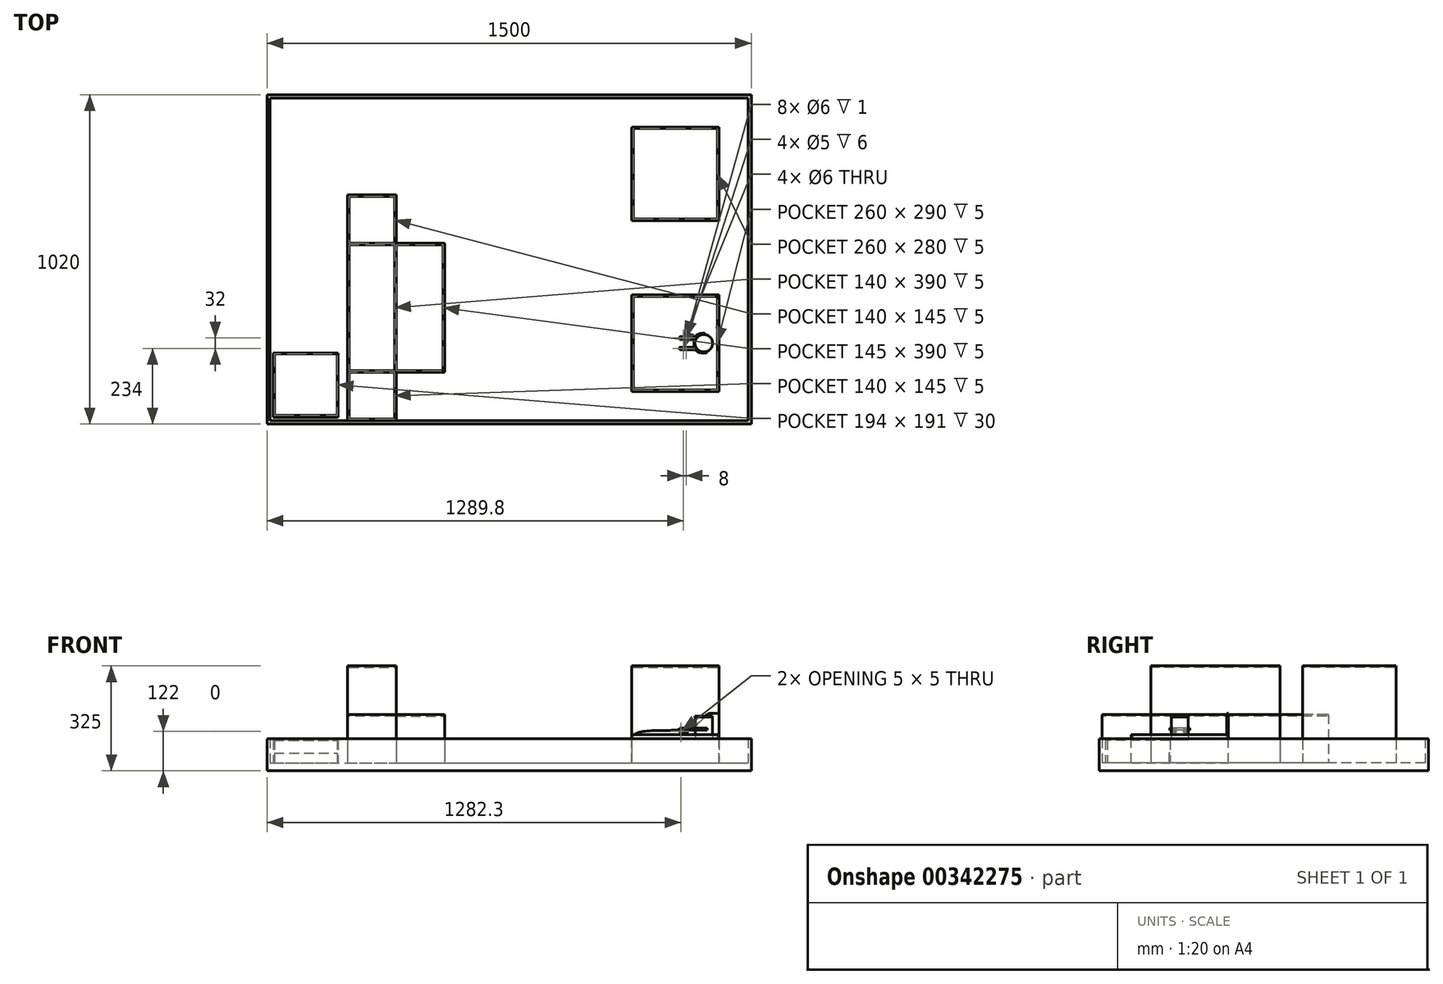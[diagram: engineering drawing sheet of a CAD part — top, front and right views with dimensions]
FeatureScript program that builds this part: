
annotation { "Feature Type Name" : "Feature", "Feature Type Description" : "" }
export const myFeature = defineFeature(function(context is Context, id is Id, definition is map)
    precondition{}
    {
        {
            var Q0;
            Q0=qCreatedBy(makeId("Top.planeOp"),FACE);
            var sketch = newSketch(context, id + "F0", { "sketchPlane" : qUnion([Q0])});
            skCircle(sketch, "E0", {"center": v(0, 0) * mm, "radius": 27.2 * mm});
            skSolve(sketch);
        }
        {
            var Q0;
            Q0=qSketchRegion(id+"F0",true);
            extrude(context, id + "F1", {"entities" : qUnion([Q0]), "depth" : 2.83 * mm});
        }
        {
            var Q0;
            Q0=makeQuery(id+"F1.opExtrude","CAP_FACE",FACE,{"disambiguationData":[OSD([sQuery(id+"F0.wireOp",EDGE,"E0")])],"isStart":false});
            var sketch = newSketch(context, id + "F2", { "sketchPlane" : qUnion([Q0])});
            skCircle(sketch, "E1", {"center": v(0, 0) * mm, "radius": 26.4 * mm});
            skSolve(sketch);
        }
        {
            var Q0;
            Q0=qSketchRegion(id+"F2",true);
            extrude(context, id + "F3", {"entities" : qUnion([Q0]), "operationType" : NewBodyOperationType.ADD, "depth" : 67.36 * mm});
        }
        {
            var Q0;
            Q0=makeQuery(id+"F3.opExtrude","CAP_FACE",FACE,{"disambiguationData":[OSD([sQuery(id+"F2.wireOp",EDGE,"E1")])],"isStart":false});
            var sketch = newSketch(context, id + "F4", { "sketchPlane" : qUnion([Q0])});
            skCircle(sketch, "E2", {"center": v(0, 0) * mm, "radius": 27.2 * mm});
            skSolve(sketch);
        }
        {
            var Q0;
            Q0=qSketchRegion(id+"F4",true);
            extrude(context, id + "F5", {"entities" : qUnion([Q0]), "operationType" : NewBodyOperationType.ADD, "depth" : 2.83 * mm});
        }
        {
            var Q0;
            Q0=makeQuery(id+"F5.opExtrude","CAP_FACE",FACE,{"disambiguationData":[OSD([sQuery(id+"F4.wireOp",EDGE,"E2")])],"isStart":false});
            var sketch = newSketch(context, id + "F6", { "sketchPlane" : qUnion([Q0])});
            skSolve(sketch);
        }
        {
            var Q0;
            Q0=qCreatedBy(makeId("Top.planeOp"),FACE);
            cPlane(context, id + "F7", {"entities" : qUnion([Q0]), "cplaneType" : CPlaneType.OFFSET, "offset" : 25 * mm, "width" : 150 * mm, "height" : 150 * mm});
        }
        {
            var Q0;
            Q0=makeQuery(id+"F6.imprint","IMPRINT",FACE,{"disambiguationData":[TD([[makeQuery(id+"F6.imprint","IMPRINT",EDGE,{"derivedFrom":makeQuery(id+"F5.opExtrude","CAP_EDGE",EDGE,{"disambiguationData":[OSD([sQuery(id+"F4.wireOp",EDGE,"E2")])],"isStart":false})}),1.0]])]});
            var sketch = newSketch(context, id + "F8", { "sketchPlane" : qUnion([Q0])});
            skSolve(sketch);
        }
        {
            var Q0;
            Q0=qCreatedBy(makeId("Top.planeOp"),FACE);
            var sketch = newSketch(context, id + "F9", { "sketchPlane" : qUnion([Q0])});
            skLineSegment(sketch, "E3.bottom", {"start": v(-222.8, -150) * mm, "end": v(47.2, -150) * mm});
            skLineSegment(sketch, "E3.top", {"start": v(-222.8, 150) * mm, "end": v(47.2, 150) * mm});
            skLineSegment(sketch, "E3.left", {"start": v(-222.8, -150) * mm, "end": v(-222.8, 150) * mm});
            skLineSegment(sketch, "E3.right", {"start": v(47.2, -150) * mm, "end": v(47.2, 150) * mm});
            skSolve(sketch);
        }
        {
            var Q0;
            Q0=qSketchRegion(id+"F9",true);
            extrude(context, id + "F10", {"entities" : qUnion([Q0]), "oppositeDirection" : true, "depth" : 72 * mm});
        }
        {
            var Q0;
            Q0=makeQuery(id+"F10.opExtrude","CAP_FACE",FACE,{"disambiguationData":[OSD([sQuery(id+"F9.wireOp",EDGE,"E3.bottom"),sQuery(id+"F9.wireOp",EDGE,"E3.top"),sQuery(id+"F9.wireOp",EDGE,"E3.left"),sQuery(id+"F9.wireOp",EDGE,"E3.right")])],"isStart":true});
            var sketch = newSketch(context, id + "F11", { "sketchPlane" : qUnion([Q0])});
            skLineSegment(sketch, "E4.bottom", {"start": v(-222.8, -150) * mm, "end": v(47.2, -150) * mm});
            skLineSegment(sketch, "E4.top", {"start": v(-222.8, -145) * mm, "end": v(42.2, -145) * mm});
            skLineSegment(sketch, "E4.left", {"start": v(-222.8, -150) * mm, "end": v(-222.8, -145) * mm});
            skLineSegment(sketch, "E5.bottom", {"start": v(47.2, 150) * mm, "end": v(42.2, 150) * mm});
            skLineSegment(sketch, "E5.left", {"start": v(47.2, 150) * mm, "end": v(47.2, -150) * mm});
            skLineSegment(sketch, "E5.right", {"start": v(42.2, 150) * mm, "end": v(42.2, -145) * mm});
            skSolve(sketch);
        }
        {
            var Q0;
            Q0=qSketchRegion(id+"F11",true);
            extrude(context, id + "F12", {"entities" : qUnion([Q0]), "operationType" : NewBodyOperationType.ADD, "depth" : 15 * mm});
        }
        {
            var Q0;
            Q0=makeQuery(id+"F12.boolean.opBoolean","MERGE",FACE,{"derivedFrom":[makeQuery(id+"F10.opExtrude","SWEPT_FACE",FACE,{"disambiguationData":[OSD([sQuery(id+"F9.wireOp",EDGE,"E3.top")])]}),makeQuery(id+"F12.opExtrude","SWEPT_FACE",FACE,{"disambiguationData":[OSD([sQuery(id+"F11.wireOp",EDGE,"E5.bottom")])]})]});
            var sketch = newSketch(context, id + "F13", { "sketchPlane" : qUnion([Q0])});
            skLineSegment(sketch, "E6", {"start": v(-47.2, 81.36) * mm, "end": v(-21.31, 81.36) * mm});
            skFitSpline(sketch, "E7", {"points": [v(-21.31, 81.36) * mm, v(15.24, 52.01) * mm, v(114.14, 28.17) * mm, v(222.8, 0) * mm], "startDerivative": vector(181.02, 0.3) * mm, "endDerivative": vector(-1.73, -239.85) * mm});
            skLineSegment(sketch, "E8", {"start": v(-47.2, 81.36) * mm, "end": v(-47.2, -72) * mm});
            skLineSegment(sketch, "E9", {"start": v(-47.2, -72) * mm, "end": v(222.8, -72) * mm});
            skLineSegment(sketch, "E10", {"start": v(222.8, -72) * mm, "end": v(222.8, 0) * mm});
            skSolve(sketch);
        }
        {
            var Q0;
            Q0=qSketchRegion(id+"F13",true);
            extrude(context, id + "F14", {"entities" : qUnion([Q0]), "operationType" : NewBodyOperationType.ADD, "oppositeDirection" : true, "depth" : 5 * mm});
        }
        {
            var Q0;
            Q0=makeQuery(id+"F10.opExtrude","CAP_FACE",FACE,{"disambiguationData":[OSD([sQuery(id+"F9.wireOp",EDGE,"E3.bottom"),sQuery(id+"F9.wireOp",EDGE,"E3.top"),sQuery(id+"F9.wireOp",EDGE,"E3.left"),sQuery(id+"F9.wireOp",EDGE,"E3.right")])],"isStart":true});
            var sketch = newSketch(context, id + "F15", { "sketchPlane" : qUnion([Q0])});
            skLineSegment(sketch, "E11.bottom", {"start": v(-222.8, 145) * mm, "end": v(-217.8, 145) * mm});
            skLineSegment(sketch, "E11.top", {"start": v(-222.8, -145) * mm, "end": v(-217.8, -145) * mm});
            skLineSegment(sketch, "E11.left", {"start": v(-222.8, 145) * mm, "end": v(-222.8, -145) * mm});
            skLineSegment(sketch, "E11.right", {"start": v(-217.8, 145) * mm, "end": v(-217.8, -145) * mm});
            skSolve(sketch);
        }
        {
            var Q0;
            Q0=qSketchRegion(id+"F15",true);
            extrude(context, id + "F16", {"entities" : qUnion([Q0]), "operationType" : NewBodyOperationType.ADD, "depth" : 5 * mm});
        }
        {
            var Q0;
            Q0=makeQuery(id+"F10.opExtrude","CAP_FACE",FACE,{"disambiguationData":[OSD([sQuery(id+"F9.wireOp",EDGE,"E3.bottom"),sQuery(id+"F9.wireOp",EDGE,"E3.top"),sQuery(id+"F9.wireOp",EDGE,"E3.left"),sQuery(id+"F9.wireOp",EDGE,"E3.right")])],"isStart":false});
            var sketch = newSketch(context, id + "F17", { "sketchPlane" : qUnion([Q0])});
            skLineSegment(sketch, "E12.bottom", {"start": v(147.2, 250) * mm, "end": v(-1352.8, 250) * mm});
            skLineSegment(sketch, "E12.top", {"start": v(147.2, -770) * mm, "end": v(-1352.8, -770) * mm});
            skLineSegment(sketch, "E12.left", {"start": v(147.2, 250) * mm, "end": v(147.2, -770) * mm});
            skLineSegment(sketch, "E12.right", {"start": v(-1352.8, 250) * mm, "end": v(-1352.8, -770) * mm});
            skSolve(sketch);
        }
        {
            var Q0;
            Q0=qSketchRegion(id+"F17",true);
            extrude(context, id + "F18", {"entities" : qUnion([Q0]), "operationType" : NewBodyOperationType.ADD, "depth" : 25 * mm});
        }
        {
            var Q0;
            Q0=makeQuery(id+"F18.opExtrude","CAP_FACE",FACE,{"disambiguationData":[OSD([sQuery(id+"F17.wireOp",EDGE,"E12.bottom"),sQuery(id+"F17.wireOp",EDGE,"E12.top"),sQuery(id+"F17.wireOp",EDGE,"E12.left"),sQuery(id+"F17.wireOp",EDGE,"E12.right")])],"isStart":true});
            var sketch = newSketch(context, id + "F19", { "sketchPlane" : qUnion([Q0])});
            skLineSegment(sketch, "E13.bottom", {"start": v(-222.8, 670) * mm, "end": v(47.2, 670) * mm});
            skLineSegment(sketch, "E13.top", {"start": v(-222.8, 380) * mm, "end": v(47.2, 380) * mm});
            skLineSegment(sketch, "E13.left", {"start": v(-222.8, 670) * mm, "end": v(-222.8, 380) * mm});
            skLineSegment(sketch, "E13.right", {"start": v(47.2, 670) * mm, "end": v(47.2, 380) * mm});
            skSolve(sketch);
        }
        {
            var Q0;
            Q0=qSketchRegion(id+"F19",true);
            extrude(context, id + "F20", {"entities" : qUnion([Q0]), "operationType" : NewBodyOperationType.ADD, "depth" : 300 * mm});
        }
        {
            var Q0;
            Q0=makeQuery(id+"F20.opExtrude","CAP_FACE",FACE,{"disambiguationData":[OSD([sQuery(id+"F19.wireOp",EDGE,"E13.bottom"),sQuery(id+"F19.wireOp",EDGE,"E13.top"),sQuery(id+"F19.wireOp",EDGE,"E13.left"),sQuery(id+"F19.wireOp",EDGE,"E13.right")])],"isStart":false});
            var sketch = newSketch(context, id + "F21", { "sketchPlane" : qUnion([Q0])});
            skLineSegment(sketch, "E14.bottom", {"start": v(-217.8, 665) * mm, "end": v(42.2, 665) * mm});
            skLineSegment(sketch, "E14.top", {"start": v(-217.8, 385) * mm, "end": v(42.2, 385) * mm});
            skLineSegment(sketch, "E14.left", {"start": v(-217.8, 665) * mm, "end": v(-217.8, 385) * mm});
            skLineSegment(sketch, "E14.right", {"start": v(42.2, 665) * mm, "end": v(42.2, 385) * mm});
            skSolve(sketch);
        }
        {
            var Q0;
            Q0=qSketchRegion(id+"F21",true);
            extrude(context, id + "F22", {"entities" : qUnion([Q0]), "operationType" : NewBodyOperationType.REMOVE, "oppositeDirection" : true, "depth" : 5 * mm});
        }
        {
            var Q0;
            Q0=makeQuery(id+"F18.opExtrude","CAP_FACE",FACE,{"disambiguationData":[OSD([sQuery(id+"F17.wireOp",EDGE,"E12.bottom"),sQuery(id+"F17.wireOp",EDGE,"E12.top"),sQuery(id+"F17.wireOp",EDGE,"E12.left"),sQuery(id+"F17.wireOp",EDGE,"E12.right")])],"isStart":true});
            var sketch = newSketch(context, id + "F23", { "sketchPlane" : qUnion([Q0])});
            skLineSegment(sketch, "E15.bottom", {"start": v(-1352.8, 770) * mm, "end": v(147.2, 770) * mm});
            skLineSegment(sketch, "E15.top", {"start": v(-1352.8, -250) * mm, "end": v(147.2, -250) * mm});
            skLineSegment(sketch, "E15.left", {"start": v(-1352.8, 770) * mm, "end": v(-1352.8, -250) * mm});
            skLineSegment(sketch, "E15.right", {"start": v(147.2, 770) * mm, "end": v(147.2, -250) * mm});
            skLineSegment(sketch, "E16.bottom", {"start": v(-1342.8, 760) * mm, "end": v(137.2, 760) * mm});
            skLineSegment(sketch, "E16.top", {"start": v(-1342.8, -240) * mm, "end": v(137.2, -240) * mm});
            skLineSegment(sketch, "E16.left", {"start": v(-1342.8, 760) * mm, "end": v(-1342.8, -240) * mm});
            skLineSegment(sketch, "E16.right", {"start": v(137.2, 760) * mm, "end": v(137.2, -240) * mm});
            skSolve(sketch);
        }
        {
            var Q0;
            Q0=qSketchRegion(id+"F23",true);
            extrude(context, id + "F24", {"entities" : qUnion([Q0]), "operationType" : NewBodyOperationType.ADD, "depth" : 75 * mm});
        }
        {
            var Q0;
            Q0=makeQuery(id+"F18.opExtrude","CAP_FACE",FACE,{"disambiguationData":[OSD([sQuery(id+"F17.wireOp",EDGE,"E12.bottom"),sQuery(id+"F17.wireOp",EDGE,"E12.top"),sQuery(id+"F17.wireOp",EDGE,"E12.left"),sQuery(id+"F17.wireOp",EDGE,"E12.right")])],"isStart":true});
            var sketch = newSketch(context, id + "F25", { "sketchPlane" : qUnion([Q0])});
            skLineSegment(sketch, "E17.bottom", {"start": v(-1102.8, 460) * mm, "end": v(-952.8, 460) * mm});
            skLineSegment(sketch, "E17.top", {"start": v(-1102.8, -240) * mm, "end": v(-952.8, -240) * mm});
            skLineSegment(sketch, "E17.left", {"start": v(-1102.8, 460) * mm, "end": v(-1102.8, -240) * mm});
            skLineSegment(sketch, "E17.right", {"start": v(-952.8, 460) * mm, "end": v(-952.8, 310) * mm});
            skLineSegment(sketch, "E18.bottom", {"start": v(-952.8, 310) * mm, "end": v(-802.8, 310) * mm});
            skLineSegment(sketch, "E18.top", {"start": v(-952.8, -90) * mm, "end": v(-802.8, -90) * mm});
            skLineSegment(sketch, "E18.right", {"start": v(-802.8, 310) * mm, "end": v(-802.8, -90) * mm});
            skLineSegment(sketch, "E19.trimOffspring", {"start": v(-952.8, -90) * mm, "end": v(-952.8, -240) * mm});
            skSolve(sketch);
        }
        {
            var Q0;
            Q0=qSketchRegion(id+"F25",true);
            extrude(context, id + "F26", {"entities" : qUnion([Q0]), "operationType" : NewBodyOperationType.ADD, "depth" : 150 * mm});
        }
        {
            var Q0;
            Q0=makeQuery(id+"F26.opExtrude","CAP_FACE",FACE,{"disambiguationData":[OSD([sQuery(id+"F25.wireOp",EDGE,"E17.bottom"),sQuery(id+"F25.wireOp",EDGE,"E17.top"),sQuery(id+"F25.wireOp",EDGE,"E17.left"),sQuery(id+"F25.wireOp",EDGE,"E17.right"),sQuery(id+"F25.wireOp",EDGE,"E18.bottom"),sQuery(id+"F25.wireOp",EDGE,"E18.top"),sQuery(id+"F25.wireOp",EDGE,"E18.right"),sQuery(id+"F25.wireOp",EDGE,"E19.trimOffspring")])],"isStart":false});
            var sketch = newSketch(context, id + "F27", { "sketchPlane" : qUnion([Q0])});
            skLineSegment(sketch, "E20.bottom", {"start": v(-952.8, 310) * mm, "end": v(-1102.8, 310) * mm});
            skLineSegment(sketch, "E20.top", {"start": v(-952.8, -90) * mm, "end": v(-1102.8, -90) * mm});
            skLineSegment(sketch, "E20.left", {"start": v(-952.8, 310) * mm, "end": v(-952.8, -90) * mm});
            skLineSegment(sketch, "E20.right", {"start": v(-1102.8, 310) * mm, "end": v(-1102.8, -90) * mm});
            skSolve(sketch);
        }
        {
            var Q0;
            Q0=qSketchRegion(id+"F27",true);
            extrude(context, id + "F28", {"entities" : qUnion([Q0]), "operationType" : NewBodyOperationType.ADD, "depth" : 150 * mm});
        }
        {
            var Q0;
            Q0=makeQuery(id+"F28.opExtrude","CAP_FACE",FACE,{"disambiguationData":[OSD([sQuery(id+"F27.wireOp",EDGE,"E20.bottom"),sQuery(id+"F27.wireOp",EDGE,"E20.top"),sQuery(id+"F27.wireOp",EDGE,"E20.left"),sQuery(id+"F27.wireOp",EDGE,"E20.right")])],"isStart":false});
            var sketch = newSketch(context, id + "F29", { "sketchPlane" : qUnion([Q0])});
            skLineSegment(sketch, "E21.bottom", {"start": v(-1097.8, 305) * mm, "end": v(-957.8, 305) * mm});
            skLineSegment(sketch, "E21.top", {"start": v(-1097.8, -85) * mm, "end": v(-957.8, -85) * mm});
            skLineSegment(sketch, "E21.left", {"start": v(-1097.8, 305) * mm, "end": v(-1097.8, -85) * mm});
            skLineSegment(sketch, "E21.right", {"start": v(-957.8, 305) * mm, "end": v(-957.8, -85) * mm});
            skSolve(sketch);
        }
        {
            var Q0;
            Q0=qSketchRegion(id+"F29",true);
            extrude(context, id + "F30", {"entities" : qUnion([Q0]), "operationType" : NewBodyOperationType.REMOVE, "oppositeDirection" : true, "depth" : 5 * mm});
        }
        {
            var Q0;
            {var subQ0=sQuery(id+"F25.wireOp",EDGE,"E17.left");var subQ1=sQuery(id+"F25.wireOp",EDGE,"E18.bottom");var subQ2=sQuery(id+"F25.wireOp",EDGE,"E17.right");var subQ3=sQuery(id+"F25.wireOp",EDGE,"E17.bottom");var subQ4=makeQuery(id+"F26.opExtrude","CAP_FACE",FACE,{"disambiguationData":[OSD([subQ3,sQuery(id+"F25.wireOp",EDGE,"E17.top"),subQ0,subQ2,subQ1,sQuery(id+"F25.wireOp",EDGE,"E18.top"),sQuery(id+"F25.wireOp",EDGE,"E18.right"),sQuery(id+"F25.wireOp",EDGE,"E19.trimOffspring")])],"isStart":false});Q0=makeQuery(id+"F28.boolean.opBoolean","SPLIT",FACE,{"disambiguationData":[TD([makeQuery(id+"F26.opExtrude","SWEPT_FACE",FACE,{"disambiguationData":[OSD([subQ3])]})])],"derivedFrom":subQ4});}
            var sketch = newSketch(context, id + "F31", { "sketchPlane" : qUnion([Q0])});
            skLineSegment(sketch, "E22.bottom", {"start": v(-1097.8, 455) * mm, "end": v(-957.8, 455) * mm});
            skLineSegment(sketch, "E22.top", {"start": v(-1097.8, 310) * mm, "end": v(-957.8, 310) * mm});
            skLineSegment(sketch, "E22.left", {"start": v(-1097.8, 455) * mm, "end": v(-1097.8, 310) * mm});
            skLineSegment(sketch, "E22.right", {"start": v(-957.8, 455) * mm, "end": v(-957.8, 310) * mm});
            skLineSegment(sketch, "E23.bottom", {"start": v(-952.8, 305) * mm, "end": v(-807.8, 305) * mm});
            skLineSegment(sketch, "E23.top", {"start": v(-952.8, -85) * mm, "end": v(-807.8, -85) * mm});
            skLineSegment(sketch, "E23.left", {"start": v(-952.8, 305) * mm, "end": v(-952.8, -85) * mm});
            skLineSegment(sketch, "E23.right", {"start": v(-807.8, 305) * mm, "end": v(-807.8, -85) * mm});
            skLineSegment(sketch, "E24.bottom", {"start": v(-1097.8, -90) * mm, "end": v(-957.8, -90) * mm});
            skLineSegment(sketch, "E24.top", {"start": v(-1097.8, -235) * mm, "end": v(-957.8, -235) * mm});
            skLineSegment(sketch, "E24.left", {"start": v(-1097.8, -90) * mm, "end": v(-1097.8, -235) * mm});
            skLineSegment(sketch, "E24.right", {"start": v(-957.8, -90) * mm, "end": v(-957.8, -235) * mm});
            skSolve(sketch);
        }
        {
            var Q0;
            Q0=qSketchRegion(id+"F31",true);
            extrude(context, id + "F32", {"entities" : qUnion([Q0]), "operationType" : NewBodyOperationType.REMOVE, "oppositeDirection" : true, "depth" : 5 * mm});
        }
        {
            var Q0;
            Q0=qCreatedBy(id+"F7.planeOp",FACE);
            var sketch = newSketch(context, id + "F33", { "sketchPlane" : qUnion([Q0])});
            skLineSegment(sketch, "E25", {"start": v(0, 0) * mm, "end": v(-90, 0) * mm, "construction": true});
            skLineSegment(sketch, "E26.bottom", {"start": v(-74.5, -12) * mm, "end": v(-55, -12) * mm});
            skLineSegment(sketch, "E26.top", {"start": v(-74.5, -20) * mm, "end": v(-55, -20) * mm});
            skLineSegment(sketch, "E26.left", {"start": v(-74.5, -12) * mm, "end": v(-74.5, -13) * mm});
            skPoint(sketch, "E27.visualSharp", {"position": v(-51, -12) * mm});
            skPoint(sketch, "E28.visualSharp", {"position": v(-51, -20) * mm});
            skCircle(sketch, "E29", {"center": v(-55, -16) * mm, "radius": 3 * mm});
            skLineSegment(sketch, "E30", {"start": v(-59, -3.98) * mm, "end": v(-59, -18.08) * mm, "construction": true});
            skCircle(sketch, "E31.MirrorC", {"center": v(-63, -16) * mm, "radius": 3 * mm});
            skLineSegment(sketch, "E32.bottom", {"start": v(-74.5, -13) * mm, "end": v(-65.65, -13) * mm});
            skLineSegment(sketch, "E32.top", {"start": v(-74.5, -19) * mm, "end": v(-65.65, -19) * mm});
            skArc(sketch, "E33", {"start": v(-65.65, -13) * mm, "mid": v(-67, -16) * mm, "end": v(-65.65, -19) * mm});
            skLineSegment(sketch, "E34.trimOffspring", {"start": v(-74.5, -19) * mm, "end": v(-74.5, -20) * mm});
            skArc(sketch, "E35.trimOffspring", {"start": v(-55, -20) * mm, "mid": v(-51, -16) * mm, "end": v(-55, -12) * mm});
            skLineSegment(sketch, "E36.MirrorCS", {"start": v(-74.5, 12) * mm, "end": v(-74.5, 13) * mm});
            skLineSegment(sketch, "E37.MirrorCS", {"start": v(-74.5, 19) * mm, "end": v(-74.5, 20) * mm});
            skPoint(sketch, "E38.MirrorP", {"position": v(-51, 12) * mm});
            skLineSegment(sketch, "E39.MirrorCS", {"start": v(-74.5, 12) * mm, "end": v(-55, 12) * mm});
            skPoint(sketch, "E40.MirrorP", {"position": v(-51, 20) * mm});
            skArc(sketch, "E41.MirrorCS", {"start": v(-65.65, 13) * mm, "mid": v(-67, 16) * mm, "end": v(-65.65, 19) * mm});
            skArc(sketch, "E42.MirrorCS", {"start": v(-55, 20) * mm, "mid": v(-51, 16) * mm, "end": v(-55, 12) * mm});
            skLineSegment(sketch, "E43.MirrorCS", {"start": v(-74.5, 20) * mm, "end": v(-55, 20) * mm});
            skCircle(sketch, "E44.MirrorC", {"center": v(-55, 16) * mm, "radius": 3 * mm});
            skCircle(sketch, "E45.MirrorC", {"center": v(-63, 16) * mm, "radius": 3 * mm});
            skLineSegment(sketch, "E46.MirrorCS", {"start": v(-74.5, 19) * mm, "end": v(-65.65, 19) * mm});
            skLineSegment(sketch, "E47.MirrorCS", {"start": v(-74.5, 13) * mm, "end": v(-65.65, 13) * mm});
            skSolve(sketch);
        }
        {
            var Q0;
            Q0=qSketchRegion(id+"F33",true);
            var Q1;
            Q1=qSketchRegion(id+"F36",true);
            extrude(context, id + "F34", {"entities" : qUnion([Q0, Q1]), "endBound" : BoundingType.SYMMETRIC, "depth" : 8 * mm});
        }
        {
            var Q0;
            Q0=makeQuery(id+"F34.opExtrude","CAP_EDGE",EDGE,{"disambiguationData":[OSD([sQuery(id+"F33.wireOp",EDGE,"E34.trimOffspring")])],"isStart":false});
            var Q1;
            Q1=makeQuery(id+"F34.opExtrude","CAP_EDGE",EDGE,{"disambiguationData":[OSD([sQuery(id+"F33.wireOp",EDGE,"E26.left")])],"isStart":false});
            var Q2;
            Q2=makeQuery(id+"F34.opExtrude","CAP_EDGE",EDGE,{"disambiguationData":[OSD([sQuery(id+"F33.wireOp",EDGE,"E34.trimOffspring")])],"isStart":true});
            var Q3;
            Q3=makeQuery(id+"F34.opExtrude","CAP_EDGE",EDGE,{"disambiguationData":[OSD([sQuery(id+"F33.wireOp",EDGE,"E26.left")])],"isStart":true});
            var Q4;
            Q4=makeQuery(id+"F34.opExtrude","CAP_EDGE",EDGE,{"disambiguationData":[OSD([sQuery(id+"F33.wireOp",EDGE,"E36.MirrorCS")])],"isStart":false});
            var Q5;
            Q5=makeQuery(id+"F34.opExtrude","CAP_EDGE",EDGE,{"disambiguationData":[OSD([sQuery(id+"F33.wireOp",EDGE,"E37.MirrorCS")])],"isStart":false});
            var Q6;
            Q6=makeQuery(id+"F34.opExtrude","CAP_EDGE",EDGE,{"disambiguationData":[OSD([sQuery(id+"F33.wireOp",EDGE,"E37.MirrorCS")])],"isStart":true});
            var Q7;
            Q7=makeQuery(id+"F34.opExtrude","CAP_EDGE",EDGE,{"disambiguationData":[OSD([sQuery(id+"F33.wireOp",EDGE,"E36.MirrorCS")])],"isStart":true});
            fillet(context, id + "F35", {"entities" : qUnion([Q0, Q1, Q2, Q3, Q4, Q5, Q6, Q7]), "radius" : 4 * mm, "tangentPropagation" : true, "allowEdgeOverflow" : false});
        }
        {
            var Q0;
            Q0=makeQuery(id+"F34.opExtrude","SWEPT_FACE",FACE,{"disambiguationData":[OSD([sQuery(id+"F33.wireOp",EDGE,"E26.top")])]});
            var sketch = newSketch(context, id + "F36", { "sketchPlane" : qUnion([Q0])});
            skCircle(sketch, "E48", {"center": v(-70.5, 25) * mm, "radius": 3 * mm});
            skSolve(sketch);
        }
        {
            var Q0;
            Q0=qSketchRegion(id+"F36",true);
            var Q1;
            Q1=makeQuery(id+"F34.opExtrude","SWEPT_FACE",FACE,{"disambiguationData":[OSD([sQuery(id+"F33.wireOp",EDGE,"E26.bottom")])]});
            extrude(context, id + "F37", {"entities" : qUnion([Q0]), "operationType" : NewBodyOperationType.ADD, "endBound" : BoundingType.UP_TO_SURFACE, "oppositeDirection" : true, "endBoundEntityFace" : qUnion([Q1]), "depth" : 25 * mm});
        }
        {
            var Q0;
            Q0=makeQuery(id+"F34.opExtrude","SWEPT_FACE",FACE,{"disambiguationData":[OSD([sQuery(id+"F33.wireOp",EDGE,"E43.MirrorCS")])]});
            var sketch = newSketch(context, id + "F38", { "sketchPlane" : qUnion([Q0])});
            skCircle(sketch, "E49", {"center": v(70.5, 25) * mm, "radius": 3 * mm});
            skSolve(sketch);
        }
        {
            var Q0;
            Q0=qSketchRegion(id+"F38",true);
            var Q1;
            Q1=makeQuery(id+"F34.opExtrude","SWEPT_FACE",FACE,{"disambiguationData":[OSD([sQuery(id+"F33.wireOp",EDGE,"E39.MirrorCS")])]});
            extrude(context, id + "F39", {"entities" : qUnion([Q0]), "operationType" : NewBodyOperationType.ADD, "endBound" : BoundingType.UP_TO_SURFACE, "oppositeDirection" : true, "endBoundEntityFace" : qUnion([Q1]), "depth" : 25 * mm});
        }
        {
            var Q0;
            Q0=qCreatedBy(id+"F7.planeOp",FACE);
            var sketch = newSketch(context, id + "F40", { "sketchPlane" : qUnion([Q0])});
            skCircle(sketch, "E50", {"center": v(-55, 16) * mm, "radius": 3 * mm});
            skCircle(sketch, "E51", {"center": v(-63, 16) * mm, "radius": 2.5 * mm});
            skCircle(sketch, "E52", {"center": v(-63, 16) * mm, "radius": 3 * mm});
            skCircle(sketch, "E53", {"center": v(-55, 16) * mm, "radius": 2.5 * mm});
            skSolve(sketch);
        }
        {
            var Q0;
            Q0=qSketchRegion(id+"F40",true);
            extrude(context, id + "F41", {"entities" : qUnion([Q0]), "operationType" : NewBodyOperationType.ADD, "endBound" : BoundingType.SYMMETRIC, "depth" : 6 * mm});
        }
        {
            var Q0;
            Q0=qCreatedBy(id+"F7.planeOp",FACE);
            var sketch = newSketch(context, id + "F42", { "sketchPlane" : qUnion([Q0])});
            skCircle(sketch, "E54", {"center": v(-63, -16) * mm, "radius": 2.5 * mm});
            skCircle(sketch, "E55", {"center": v(-63, -16) * mm, "radius": 3 * mm});
            skCircle(sketch, "E56", {"center": v(-55, -16) * mm, "radius": 2.5 * mm});
            skCircle(sketch, "E57", {"center": v(-55, -16) * mm, "radius": 3 * mm});
            skSolve(sketch);
        }
        {
            var Q0;
            Q0=qSketchRegion(id+"F42",true);
            extrude(context, id + "F43", {"entities" : qUnion([Q0]), "operationType" : NewBodyOperationType.ADD, "endBound" : BoundingType.SYMMETRIC, "depth" : 6 * mm});
        }
        {
            var Q0;
            Q0=makeQuery(id+"F34.opExtrude","SWEPT_FACE",FACE,{"disambiguationData":[OSD([sQuery(id+"F33.wireOp",EDGE,"E43.MirrorCS")])]});
            var sketch = newSketch(context, id + "F44", { "sketchPlane" : qUnion([Q0])});
            skArc(sketch, "E58", {"start": v(71.5, 27.3) * mm, "mid": v(70.5, 27.5) * mm, "end": v(69.5, 27.3) * mm});
            skLineSegment(sketch, "E59.bottom", {"start": v(68.2, 26) * mm, "end": v(69.5, 26) * mm});
            skLineSegment(sketch, "E59.top", {"start": v(68.2, 24) * mm, "end": v(69.5, 24) * mm});
            skLineSegment(sketch, "E60.left", {"start": v(71.5, 27.3) * mm, "end": v(71.5, 26) * mm});
            skLineSegment(sketch, "E60.right", {"start": v(69.5, 27.3) * mm, "end": v(69.5, 26) * mm});
            skPoint(sketch, "E61.orphan", {"position": v(69.5, 27.8) * mm});
            skPoint(sketch, "E62.orphan", {"position": v(71.5, 27.8) * mm});
            skArc(sketch, "E63.trimOffspring", {"start": v(68.2, 26) * mm, "mid": v(68, 25) * mm, "end": v(68.2, 24) * mm});
            skPoint(sketch, "E59.left.start.orphan", {"position": v(67.32, 26) * mm});
            skPoint(sketch, "E64.orphan", {"position": v(67.32, 24) * mm});
            skArc(sketch, "E65.trimOffspring", {"start": v(69.5, 22.7) * mm, "mid": v(70.5, 22.5) * mm, "end": v(71.5, 22.7) * mm});
            skLineSegment(sketch, "E66.trimOffspring", {"start": v(69.5, 24) * mm, "end": v(69.5, 22.7) * mm});
            skLineSegment(sketch, "E67.trimOffspring", {"start": v(71.5, 26) * mm, "end": v(72.8, 26) * mm});
            skLineSegment(sketch, "E68.trimOffspring", {"start": v(71.5, 24) * mm, "end": v(71.5, 22.7) * mm});
            skLineSegment(sketch, "E69.trimOffspring", {"start": v(71.5, 24) * mm, "end": v(72.8, 24) * mm});
            skPoint(sketch, "E60.top.end.orphan", {"position": v(69.5, 22.2) * mm});
            skPoint(sketch, "E70.orphan", {"position": v(71.5, 22.2) * mm});
            skPoint(sketch, "E59.right.end.orphan", {"position": v(73.68, 24) * mm});
            skPoint(sketch, "E71.orphan", {"position": v(73.68, 26) * mm});
            skArc(sketch, "E72.trimOffspring", {"start": v(72.8, 24) * mm, "mid": v(73, 25) * mm, "end": v(72.8, 26) * mm});
            skSolve(sketch);
        }
        {
            var Q0;
            Q0=qSketchRegion(id+"F44",true);
            extrude(context, id + "F45", {"entities" : qUnion([Q0]), "operationType" : NewBodyOperationType.REMOVE, "endBound" : BoundingType.THROUGH_ALL, "oppositeDirection" : true, "depth" : 25 * mm});
        }
        {
            var Q0;
            Q0=makeQuery(id+"F18.opExtrude","CAP_FACE",FACE,{"disambiguationData":[OSD([sQuery(id+"F17.wireOp",EDGE,"E12.bottom"),sQuery(id+"F17.wireOp",EDGE,"E12.top"),sQuery(id+"F17.wireOp",EDGE,"E12.left"),sQuery(id+"F17.wireOp",EDGE,"E12.right")])],"isStart":true});
            var sketch = newSketch(context, id + "F46", { "sketchPlane" : qUnion([Q0])});
            skLineSegment(sketch, "E73.bottom", {"start": v(-1332.8, -30) * mm, "end": v(-1132.8, -30) * mm});
            skLineSegment(sketch, "E73.top", {"start": v(-1332.8, -230) * mm, "end": v(-1132.8, -230) * mm});
            skLineSegment(sketch, "E73.left", {"start": v(-1332.8, -30) * mm, "end": v(-1332.8, -230) * mm});
            skLineSegment(sketch, "E73.right", {"start": v(-1132.8, -30) * mm, "end": v(-1132.8, -230) * mm});
            skLineSegment(sketch, "E74.bottom", {"start": v(-1329.8, -33) * mm, "end": v(-1135.8, -33) * mm});
            skLineSegment(sketch, "E74.top", {"start": v(-1329.8, -224) * mm, "end": v(-1135.8, -224) * mm});
            skLineSegment(sketch, "E74.left", {"start": v(-1329.8, -33) * mm, "end": v(-1329.8, -224) * mm});
            skLineSegment(sketch, "E74.right", {"start": v(-1135.8, -33) * mm, "end": v(-1135.8, -224) * mm});
            skSolve(sketch);
        }
        {
            var Q0;
            Q0=qSketchRegion(id+"F46",true);
            extrude(context, id + "F47", {"entities" : qUnion([Q0]), "operationType" : NewBodyOperationType.ADD, "depth" : 30 * mm});
        }
        {
            var Q0;
            Q0=makeQuery(id+"F47.opExtrude","CAP_FACE",FACE,{"disambiguationData":[OSD([sQuery(id+"F46.wireOp",EDGE,"E73.bottom"),sQuery(id+"F46.wireOp",EDGE,"E73.top"),sQuery(id+"F46.wireOp",EDGE,"E73.left"),sQuery(id+"F46.wireOp",EDGE,"E73.right"),sQuery(id+"F46.wireOp",EDGE,"E74.bottom"),sQuery(id+"F46.wireOp",EDGE,"E74.top"),sQuery(id+"F46.wireOp",EDGE,"E74.left"),sQuery(id+"F46.wireOp",EDGE,"E74.right")])],"isStart":false});
            var sketch = newSketch(context, id + "F48", { "sketchPlane" : qUnion([Q0])});
            skLineSegment(sketch, "E75.bottom", {"start": v(-1332.8, -30) * mm, "end": v(-1329.8, -30) * mm});
            skLineSegment(sketch, "E75.top", {"start": v(-1332.8, -230) * mm, "end": v(-1329.8, -230) * mm});
            skLineSegment(sketch, "E75.left", {"start": v(-1332.8, -30) * mm, "end": v(-1332.8, -230) * mm});
            skLineSegment(sketch, "E75.right", {"start": v(-1329.8, -30) * mm, "end": v(-1329.8, -224) * mm});
            skLineSegment(sketch, "E76.bottom", {"start": v(-1329.8, -230) * mm, "end": v(-1135.8, -230) * mm});
            skLineSegment(sketch, "E76.top", {"start": v(-1329.8, -224) * mm, "end": v(-1135.8, -224) * mm});
            skLineSegment(sketch, "E77.bottom", {"start": v(-1135.8, -230) * mm, "end": v(-1132.8, -230) * mm});
            skLineSegment(sketch, "E77.top", {"start": v(-1135.8, -30) * mm, "end": v(-1132.8, -30) * mm});
            skLineSegment(sketch, "E77.left", {"start": v(-1135.8, -224) * mm, "end": v(-1135.8, -30) * mm});
            skLineSegment(sketch, "E77.right", {"start": v(-1132.8, -230) * mm, "end": v(-1132.8, -30) * mm});
            skSolve(sketch);
        }
        {
            var Q0;
            Q0=qSketchRegion(id+"F48",true);
            extrude(context, id + "F49", {"entities" : qUnion([Q0]), "operationType" : NewBodyOperationType.ADD, "depth" : 40 * mm});
        }
        {
            var Q0;
            Q0=makeQuery(id+"F34.opExtrude","CAP_FACE",FACE,{"disambiguationData":[OSD([sQuery(id+"F33.wireOp",EDGE,"E36.MirrorCS"),sQuery(id+"F33.wireOp",EDGE,"E37.MirrorCS"),sQuery(id+"F33.wireOp",EDGE,"E39.MirrorCS"),sQuery(id+"F33.wireOp",EDGE,"E41.MirrorCS"),sQuery(id+"F33.wireOp",EDGE,"E42.MirrorCS"),sQuery(id+"F33.wireOp",EDGE,"E43.MirrorCS"),sQuery(id+"F33.wireOp",EDGE,"E44.MirrorC"),sQuery(id+"F33.wireOp",EDGE,"E45.MirrorC"),sQuery(id+"F33.wireOp",EDGE,"E46.MirrorCS"),sQuery(id+"F33.wireOp",EDGE,"E47.MirrorCS")])],"isStart":false});
            var sketch = newSketch(context, id + "F50", { "sketchPlane" : qUnion([Q0])});
            skLineSegment(sketch, "E78.bottom", {"start": v(-78.97, 27.08) * mm, "end": v(-0.62, 27.08) * mm});
            skLineSegment(sketch, "E78.top", {"start": v(-78.97, -29.9) * mm, "end": v(-0.62, -29.9) * mm});
            skLineSegment(sketch, "E78.left", {"start": v(-78.97, 27.08) * mm, "end": v(-78.97, 12) * mm});
            skLineSegment(sketch, "E78.right", {"start": v(-0.62, 27.08) * mm, "end": v(-0.62, -29.9) * mm});
            skLineSegment(sketch, "E79.bottom", {"start": v(-78.97, 12) * mm, "end": v(-44.82, 12) * mm});
            skLineSegment(sketch, "E79.top", {"start": v(-78.97, -8.24) * mm, "end": v(-44.82, -8.24) * mm});
            skLineSegment(sketch, "E79.right", {"start": v(-44.82, 12) * mm, "end": v(-44.82, -8.24) * mm});
            skLineSegment(sketch, "E80.trimOffspring", {"start": v(-78.97, -8.24) * mm, "end": v(-78.97, -29.9) * mm});
            skCircle(sketch, "E81", {"center": v(-63, 16) * mm, "radius": 2.5 * mm});
            skSolve(sketch);
        }
        {
            var Q0;
            Q0=qSketchRegion(id+"F50",true);
            extrude(context, id + "F51", {"entities" : qUnion([Q0]), "depth" : 8 * mm});
        }
        {
            var Q0;
            Q0=makeQuery(id+"F51.opExtrude","SWEPT_BODY",BODY,{"disambiguationData":[OSD([sQuery(id+"F50.wireOp",EDGE,"E78.bottom"),sQuery(id+"F50.wireOp",EDGE,"E78.top"),sQuery(id+"F50.wireOp",EDGE,"E78.left"),sQuery(id+"F50.wireOp",EDGE,"E78.right"),sQuery(id+"F50.wireOp",EDGE,"E79.bottom"),sQuery(id+"F50.wireOp",EDGE,"E79.top"),sQuery(id+"F50.wireOp",EDGE,"E79.right"),sQuery(id+"F50.wireOp",EDGE,"E80.trimOffspring"),sQuery(id+"F50.wireOp",EDGE,"E81")])]});
            deleteBodies(context, id + "F52", {"entities" : qUnion([Q0])});
        }
        {
            var Q0;
            Q0=makeQuery(id+"F34.opExtrude","CAP_FACE",FACE,{"disambiguationData":[OSD([sQuery(id+"F33.wireOp",EDGE,"E36.MirrorCS"),sQuery(id+"F33.wireOp",EDGE,"E37.MirrorCS"),sQuery(id+"F33.wireOp",EDGE,"E39.MirrorCS"),sQuery(id+"F33.wireOp",EDGE,"E41.MirrorCS"),sQuery(id+"F33.wireOp",EDGE,"E42.MirrorCS"),sQuery(id+"F33.wireOp",EDGE,"E43.MirrorCS"),sQuery(id+"F33.wireOp",EDGE,"E44.MirrorC"),sQuery(id+"F33.wireOp",EDGE,"E45.MirrorC"),sQuery(id+"F33.wireOp",EDGE,"E46.MirrorCS"),sQuery(id+"F33.wireOp",EDGE,"E47.MirrorCS")])],"isStart":false});
            var sketch = newSketch(context, id + "F53", { "sketchPlane" : qUnion([Q0])});
            skLineSegment(sketch, "E82", {"start": v(-74.25, 20) * mm, "end": v(-27.6, 20) * mm});
            skLineSegment(sketch, "E83", {"start": v(-27.6, 20) * mm, "end": v(-20.19, 27.1) * mm});
            skLineSegment(sketch, "E84", {"start": v(-20.19, 27.1) * mm, "end": v(-10.42, 30.09) * mm});
            skLineSegment(sketch, "E85", {"start": v(-10.42, 30.09) * mm, "end": v(-0.8, 31.35) * mm});
            skLineSegment(sketch, "E86", {"start": v(-0.8, 31.35) * mm, "end": v(3.77, 29.61) * mm});
            skLineSegment(sketch, "E87", {"start": v(-74.25, 11.64) * mm, "end": v(-30.88, 11.64) * mm});
            skLineSegment(sketch, "E88", {"start": v(-30.88, 11.64) * mm, "end": v(-30.88, 4.4) * mm});
            skLineSegment(sketch, "E89", {"start": v(-30.88, 4.4) * mm, "end": v(-30.88, -2.54) * mm});
            skLineSegment(sketch, "E90", {"start": v(-30.88, -2.54) * mm, "end": v(-30.88, -7.59) * mm});
            skLineSegment(sketch, "E91", {"start": v(-30.88, -7.59) * mm, "end": v(-30.88, -12) * mm});
            skLineSegment(sketch, "E92", {"start": v(-30.88, -12) * mm, "end": v(-74.25, -12) * mm});
            skLineSegment(sketch, "E93", {"start": v(-74.25, 11.64) * mm, "end": v(-74.25, 20) * mm});
            skLineSegment(sketch, "E94", {"start": v(-74.25, -12) * mm, "end": v(-74.25, -20.04) * mm});
            skLineSegment(sketch, "E95", {"start": v(-74.25, -20.04) * mm, "end": v(-26.65, -20.04) * mm});
            skLineSegment(sketch, "E96", {"start": v(-26.65, -20.04) * mm, "end": v(-16.08, -28.6) * mm});
            skLineSegment(sketch, "E97", {"start": v(-16.08, -28.6) * mm, "end": v(-6.9, -31) * mm});
            skLineSegment(sketch, "E98", {"start": v(-6.9, -31) * mm, "end": v(5.3, -31) * mm});
            skLineSegment(sketch, "E99", {"start": v(5.3, -31) * mm, "end": v(10.82, -28.43) * mm});
            skLineSegment(sketch, "E100", {"start": v(3.77, 29.61) * mm, "end": v(-16.04, 24.61) * mm});
            skLineSegment(sketch, "E101", {"start": v(-16.04, 24.61) * mm, "end": v(-23.13, 18.35) * mm});
            skLineSegment(sketch, "E102", {"start": v(-23.13, 18.35) * mm, "end": v(-27.41, 11.92) * mm});
            skLineSegment(sketch, "E103", {"start": v(-27.41, 11.92) * mm, "end": v(-27.41, -12.64) * mm});
            skLineSegment(sketch, "E104", {"start": v(-27.41, -12.64) * mm, "end": v(-15.05, -24.84) * mm});
            skLineSegment(sketch, "E105", {"start": v(-15.05, -24.84) * mm, "end": v(3.77, -28.96) * mm});
            skCircle(sketch, "E106", {"center": v(-63, 16) * mm, "radius": 3 * mm});
            skCircle(sketch, "E107", {"center": v(-55, 16) * mm, "radius": 3 * mm});
            skCircle(sketch, "E108", {"center": v(-63, -16) * mm, "radius": 3 * mm});
            skCircle(sketch, "E109", {"center": v(-55, -16) * mm, "radius": 3 * mm});
            skLineSegment(sketch, "E110", {"start": v(3.77, -28.96) * mm, "end": v(10.82, -28.43) * mm});
            skSolve(sketch);
        }
        {
            var Q0;
            Q0 = qSketchRegion(id + "F53", true);
            extrude(context, id + "F54", {"entities" : qUnion([Q0]), "depth" : 6 * mm});
        }
    });
